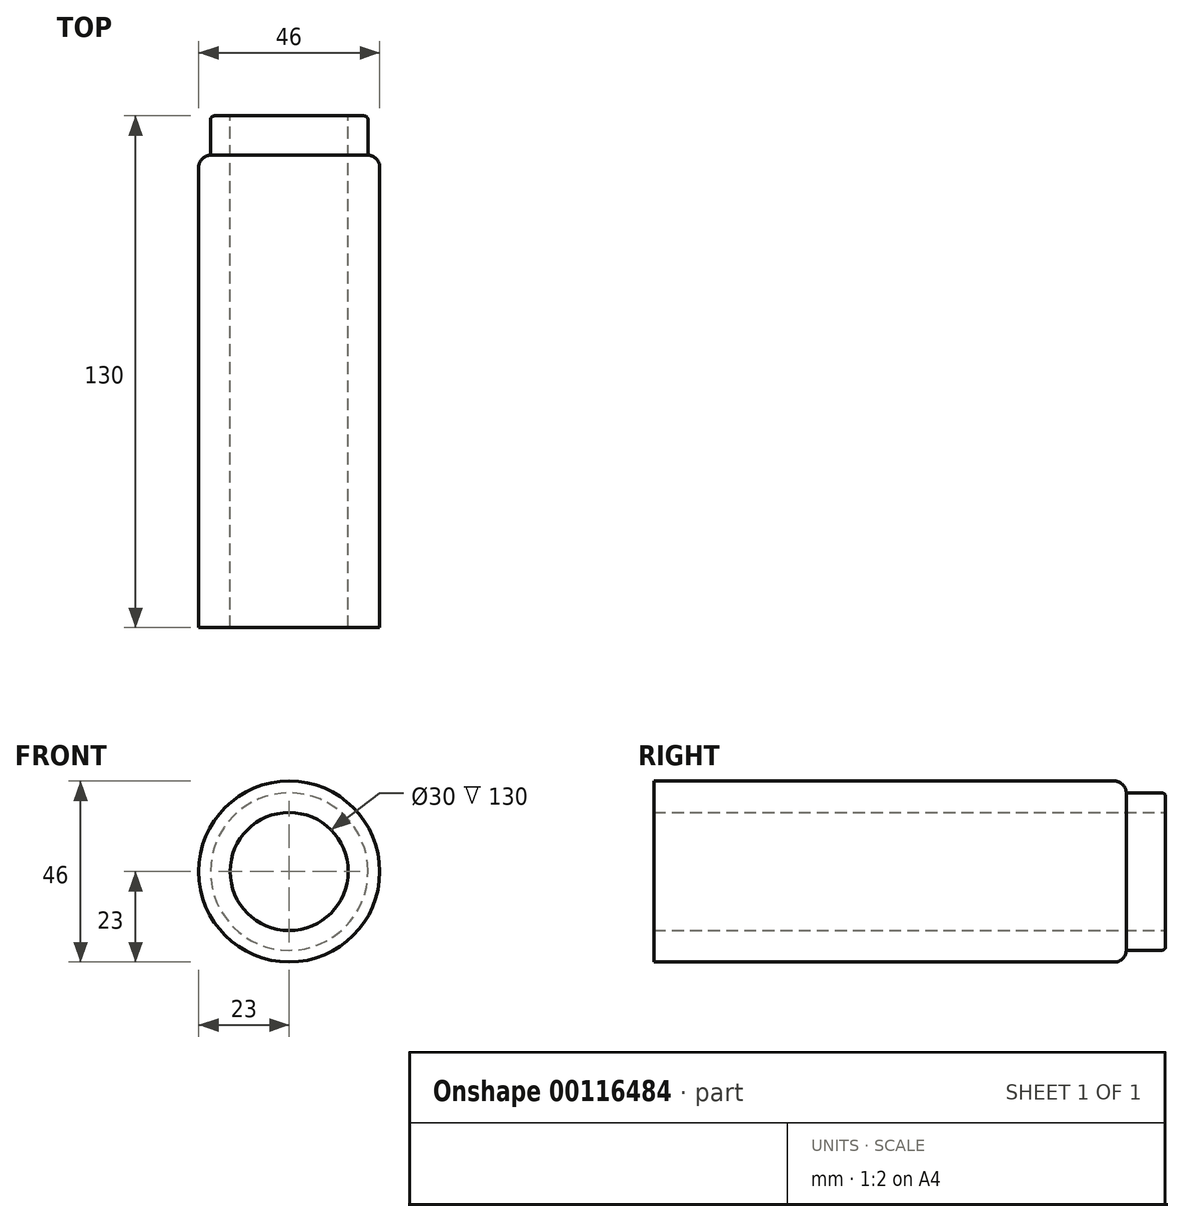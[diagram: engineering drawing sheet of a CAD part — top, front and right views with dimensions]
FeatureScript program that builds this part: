
annotation { "Feature Type Name" : "Feature", "Feature Type Description" : "" }
export const myFeature = defineFeature(function(context is Context, id is Id, definition is map)
    precondition{}
    {
        {
            var Q0;
            Q0=qCreatedBy(makeId("Front.planeOp"),FACE);
            var sketch = newSketch(context, id + "F0", { "sketchPlane" : qUnion([Q0])});
            skCircle(sketch, "E0", {"center": v(0, 0) * mm, "radius": 15 * mm});
            skCircle(sketch, "E1.0", {"center": v(0, 0) * mm, "radius": 20 * mm});
            skSolve(sketch);
        }
        {
            var Q0;
            Q0 = qSketchRegion(id + "F0", true);
            var Q1;
            Q1=makeQuery(id+"F0.imprint","IMPRINT",FACE,{"disambiguationData":[TD([[makeQuery(id+"F0.imprint","IMPRINT",EDGE,{"derivedFrom":sQuery(id+"F0.wireOp",EDGE,"E0")}),-1.0]])]});
            extrude(context, id + "F1", {"entities" : qUnion([Q0, Q1]), "endBound" : BoundingType.SYMMETRIC, "depth" : 10 * mm});
        }
        {
            var Q0;
            Q0=makeQuery(id+"F1.opExtrude","CAP_FACE",FACE,{"disambiguationData":[OSD([sQuery(id+"F0.wireOp",EDGE,"E0"),sQuery(id+"F0.wireOp",EDGE,"E1.0")])],"isStart":false});
            var sketch = newSketch(context, id + "F2", { "sketchPlane" : qUnion([Q0])});
            skCircle(sketch, "E2", {"center": v(0, 0) * mm, "radius": 15 * mm});
            skCircle(sketch, "E3.0", {"center": v(0, 0) * mm, "radius": 23 * mm});
            skSolve(sketch);
        }
        {
            var Q0;
            Q0 = qSketchRegion(id + "F2", true);
            var Q1;
            Q1=makeQuery(id+"F2.imprint","IMPRINT",FACE,{"disambiguationData":[TD([[makeQuery(id+"F2.imprint","IMPRINT",EDGE,{"derivedFrom":sQuery(id+"F2.wireOp",EDGE,"E3.0")}),1.0]])]});
            extrude(context, id + "F3", {"entities" : qUnion([Q0, Q1]), "operationType" : NewBodyOperationType.ADD, "depth" : 120 * mm});
        }
        {
            var Q0;
            Q0=makeQuery(id+"F3.opExtrude","CAP_EDGE",EDGE,{"disambiguationData":[OSD([sQuery(id+"F2.wireOp",EDGE,"E3.0")])],"isStart":true});
            fillet(context, id + "F4", {"entities" : qUnion([Q0]), "radius" : 3 * mm, "tangentPropagation" : true, "allowEdgeOverflow" : false});
        }
        {
            var Q0;
            Q0=makeQuery(id+"F1.opExtrude","CAP_EDGE",EDGE,{"disambiguationData":[OSD([sQuery(id+"F0.wireOp",EDGE,"E1.0")])],"isStart":true});
            fillet(context, id + "F5", {"entities" : qUnion([Q0]), "radius" : 1 * mm, "tangentPropagation" : true, "allowEdgeOverflow" : false});
        }
    });
